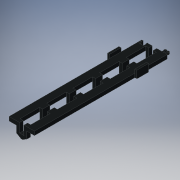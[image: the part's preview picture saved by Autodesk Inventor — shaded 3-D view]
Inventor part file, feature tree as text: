
AUTODESK INVENTOR PART (.ipt)
format: ipt  version: 2019 (Build 230136000, 136)  size: 241,152 bytes
history: native  units: mm
features: extrude x10, sketch x10, other x7
ambient origin geometry x8: Origin, YZ Plane, XZ Plane, XY Plane, X Axis, Y Axis, Z Axis, Center Point
bodies: Solid1 (feature_tree)
feature tree (27):
  extrude  "Extrusion1"  Depth=178.0mm TaperAngle=0.0deg
  extrude  "Extrusion2"  Depth=25.0mm TaperAngle=0.0deg
  extrude  "Extrusion3"  Depth=25.0mm TaperAngle=0.0deg
  extrude  "Extrusion4"  Depth=6.0mm TaperAngle=0.0deg
  extrude  "Extrusion5"  Depth=2.75mm TaperAngle=0.0deg
  extrude  "Extrusion6"  [1 undecoded]
  extrude  "Extrusion7"  [1 undecoded]
  extrude  "Extrusion8"  [1 undecoded]
  extrude  "Extrusion9"  [1 undecoded]
  extrude  "Extrusion10"  [1 undecoded]
  other  "p1_XY"
  other  "p1_YZ"
  other  "p1_ZX"
  other  "p1_X"
  other  "p1_Y"
  other  "p1_Z"
  other  "p1_Center"
  sketch  "Sketch_1"  dims[d0=178.0mm d1=0.0mm d2=25.0mm d3=0.0mm]
  sketch  "Sketch_9"  dims[d20=0.0mm]
  sketch  "Sketch_2"  dims[d4=25.0mm d5=0.0mm d6=25.0mm d7=0.0mm]
  sketch  "Sketch_3"  dims[d8=25.0mm d9=0.0mm d10=25.0mm d11=0.0mm]
  sketch  "Sketch_4"  dims[d12=2.7mm d13=0.0mm d14=6.0mm d15=0.0mm]
  sketch  "Sketch_5"  dims[d16=2.75mm d17=0.0mm d18=2.75mm d19=0.0mm]
  sketch  "Sketch_10"
  sketch  "Sketch_12"
  sketch  "Sketch_16"
  sketch  "Sketch_14"
note: 5 required parameter values undecoded (feature->parameter linkage not recoverable at this tier; creation-order binding heuristic only, values carry confidence <= 0.55)
